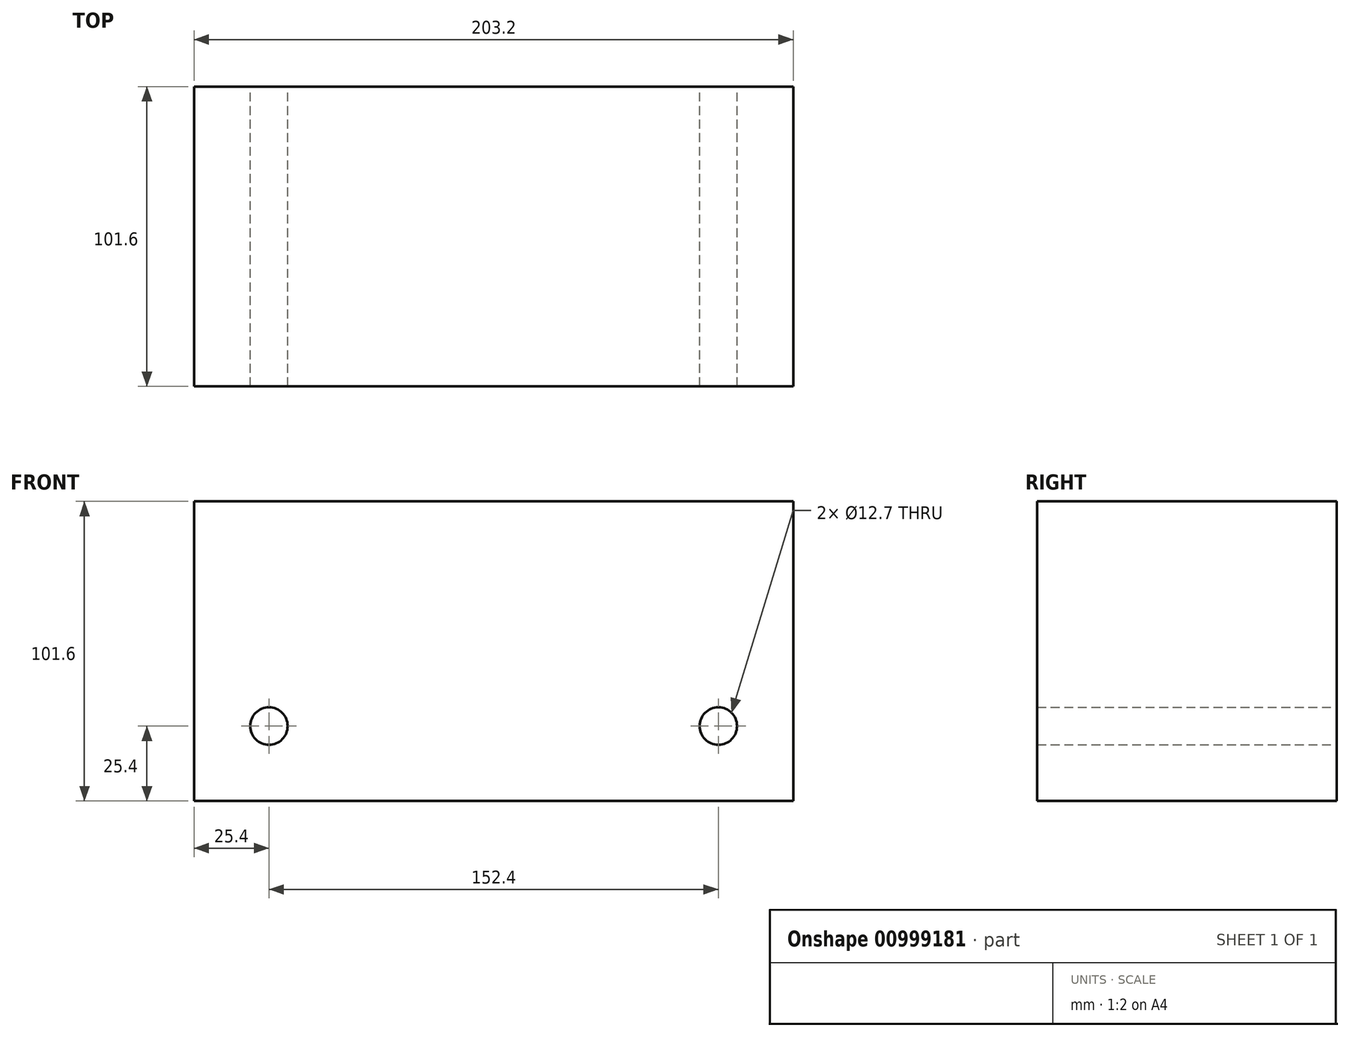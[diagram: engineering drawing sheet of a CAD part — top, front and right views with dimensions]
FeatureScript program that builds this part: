
annotation { "Feature Type Name" : "Feature", "Feature Type Description" : "" }
export const myFeature = defineFeature(function(context is Context, id is Id, definition is map)
    precondition{}
    {
        {
            var Q0;
            Q0=qCreatedBy(makeId("Front.planeOp"),FACE);
            var sketch = newSketch(context, id + "F0", { "sketchPlane" : qUnion([Q0])});
            skLineSegment(sketch, "E0.bottom", {"start": v(-101.6, 50.8) * mm, "end": v(101.6, 50.8) * mm});
            skLineSegment(sketch, "E0.top", {"start": v(-101.6, -50.8) * mm, "end": v(101.6, -50.8) * mm});
            skLineSegment(sketch, "E0.left", {"start": v(-101.6, 50.8) * mm, "end": v(-101.6, -50.8) * mm});
            skLineSegment(sketch, "E0.right", {"start": v(101.6, 50.8) * mm, "end": v(101.6, -50.8) * mm});
            skCircle(sketch, "E1", {"center": v(-76.2, -25.4) * mm, "radius": 6.35 * mm});
            skCircle(sketch, "E2", {"center": v(76.2, -25.4) * mm, "radius": 6.35 * mm});
            skSolve(sketch);
        }
        {
            var Q0;
            Q0=makeQuery(id+"F0.imprint","IMPRINT",FACE,{"disambiguationData":[TD([[makeQuery(id+"F0.imprint","IMPRINT",EDGE,{"derivedFrom":sQuery(id+"F0.wireOp",EDGE,"E0.bottom")}),-1.0]])]});
            extrude(context, id + "F1", {"entities" : qUnion([Q0]), "depth" : 101.6 * mm, "offsetDistance" : 25.4 * mm});
        }
    });
